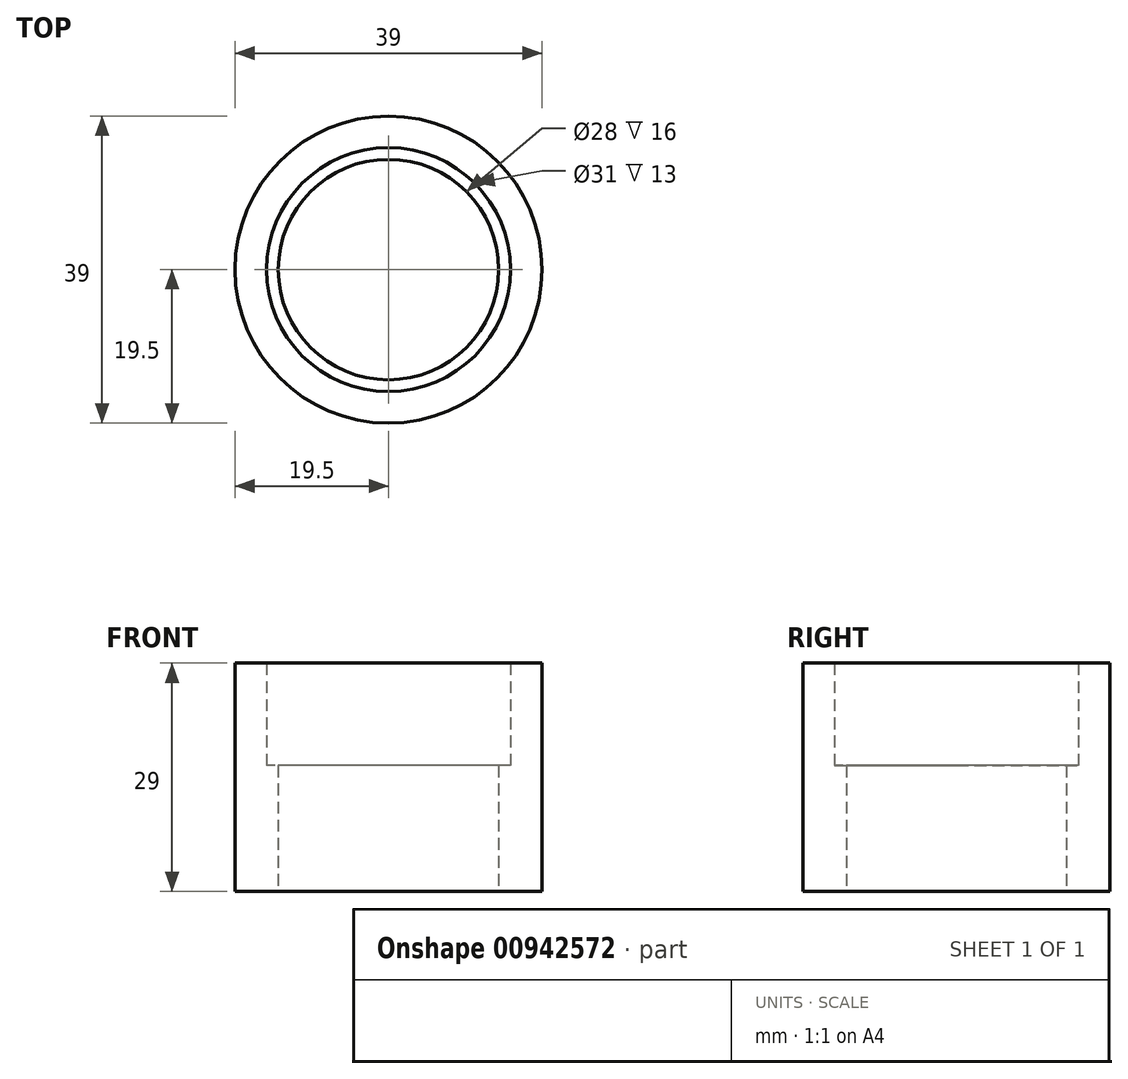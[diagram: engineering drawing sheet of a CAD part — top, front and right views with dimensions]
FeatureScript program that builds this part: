
annotation { "Feature Type Name" : "Feature", "Feature Type Description" : "" }
export const myFeature = defineFeature(function(context is Context, id is Id, definition is map)
    precondition{}
    {
        {
            var Q0;
            Q0=qCreatedBy(makeId("Top.planeOp"),FACE);
            var sketch = newSketch(context, id + "F0", { "sketchPlane" : qUnion([Q0])});
            skCircle(sketch, "E0", {"center": v(0, 0) * mm, "radius": 14 * mm});
            skCircle(sketch, "E1", {"center": v(0, 0) * mm, "radius": 18 * mm});
            skSolve(sketch);
        }
        {
            var Q0;
            Q0=qCreatedBy(makeId("Top.planeOp"),FACE);
            var sketch = newSketch(context, id + "F1", { "sketchPlane" : qUnion([Q0])});
            skCircle(sketch, "E2", {"center": v(0, 0) * mm, "radius": 15.5 * mm});
            skCircle(sketch, "E3", {"center": v(0, 0) * mm, "radius": 19.5 * mm});
            skSolve(sketch);
        }
        {
            var Q0;
            Q0=makeQuery(id+"F0.imprint","IMPRINT",FACE,{"disambiguationData":[TD([[makeQuery(id+"F0.imprint","IMPRINT",EDGE,{"derivedFrom":sQuery(id+"F0.wireOp",EDGE,"E0")}),-1.0]])]});
            extrude(context, id + "F2", {"entities" : qUnion([Q0]), "depth" : 16 * mm, "offsetDistance" : 25.4 * mm});
        }
        {
            var Q0;
            Q0=makeQuery(id+"F1.imprint","IMPRINT",FACE,{"disambiguationData":[TD([[makeQuery(id+"F1.imprint","IMPRINT",EDGE,{"derivedFrom":sQuery(id+"F1.wireOp",EDGE,"E2")}),-1.0]])]});
            extrude(context, id + "F3", {"entities" : qUnion([Q0]), "operationType" : NewBodyOperationType.ADD, "depth" : 29 * mm, "offsetDistance" : 25.4 * mm});
        }
    });
